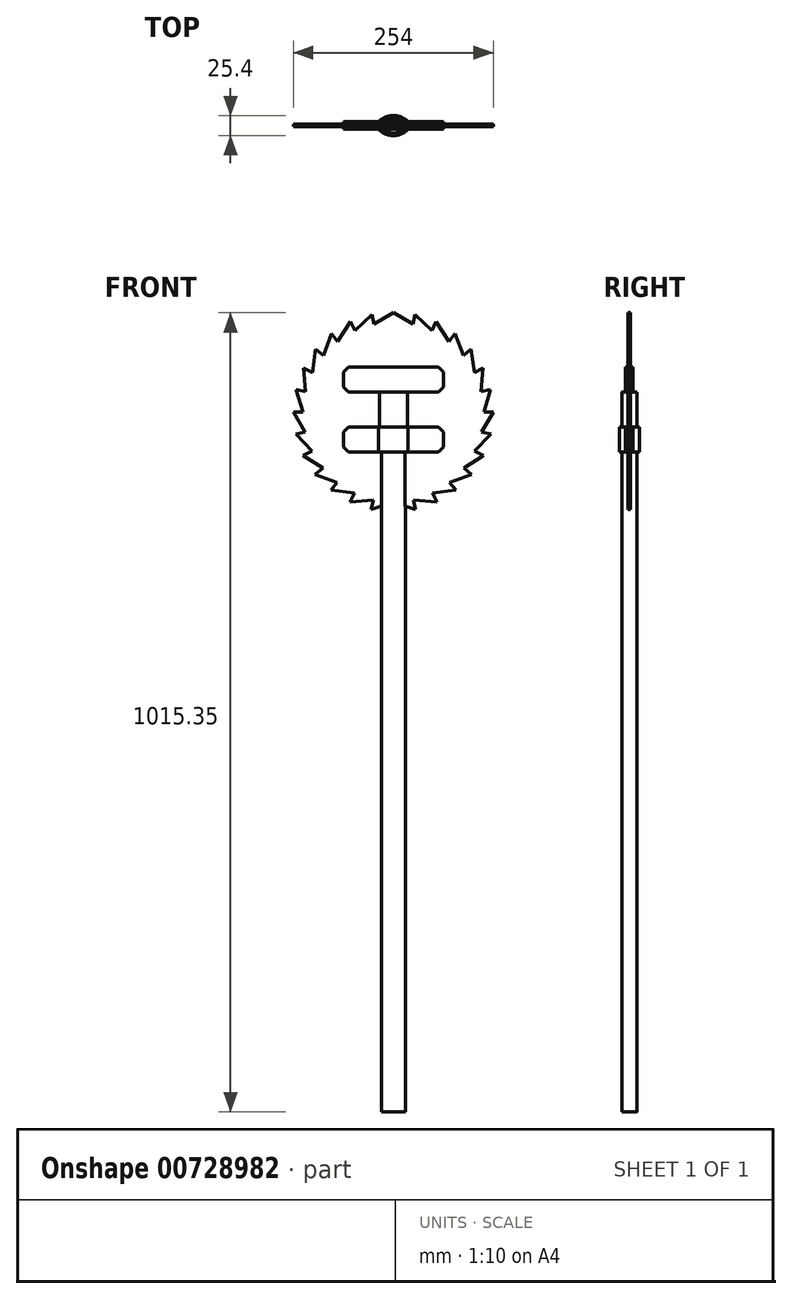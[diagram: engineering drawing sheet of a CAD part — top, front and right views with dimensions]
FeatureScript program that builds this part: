
annotation { "Feature Type Name" : "Feature", "Feature Type Description" : "" }
export const myFeature = defineFeature(function(context is Context, id is Id, definition is map)
    precondition{}
    {
        {
            var Q0;
            Q0=qCreatedBy(makeId("Top.planeOp"),FACE);
            var sketch = newSketch(context, id + "F0", { "sketchPlane" : qUnion([Q0])});
            skArc(sketch, "E0", {"start": v(19.05, 0) * mm, "mid": v(0, 9.53) * mm, "end": v(-19.05, 0) * mm});
            skArc(sketch, "E1", {"start": v(-19.05, 0) * mm, "mid": v(0, -9.53) * mm, "end": v(19.05, 0) * mm});
            skSolve(sketch);
        }
        {
            var Q0;
            Q0 = qSketchRegion(id + "F0", true);
            extrude(context, id + "F1", {"entities" : qUnion([Q0]), "depth" : 914.4 * mm, "offsetDistance" : 25.4 * mm});
        }
        {
            var Q0;
            Q0=qCreatedBy(makeId("Front.planeOp"),FACE);
            var sketch = newSketch(context, id + "F2", { "sketchPlane" : qUnion([Q0])});
            skCircle(sketch, "E2", {"center": v(0, 889) * mm, "radius": 127 * mm});
            skPoint(sketch, "E3", {"position": v(-28.3, 765.2) * mm});
            skPoint(sketch, "E4", {"position": v(0, 762) * mm});
            skPoint(sketch, "E5", {"position": v(-55.17, 774.6) * mm});
            skPoint(sketch, "E6", {"position": v(-79.26, 789.77) * mm});
            skPoint(sketch, "E7", {"position": v(-99.38, 809.93) * mm});
            skPoint(sketch, "E8", {"position": v(-114.5, 834.05) * mm});
            skPoint(sketch, "E9", {"position": v(-123.86, 860.94) * mm});
            skPoint(sketch, "E10", {"position": v(-127, 889.42) * mm});
            skPoint(sketch, "E11", {"position": v(-123.67, 917.89) * mm});
            skPoint(sketch, "E12", {"position": v(-114.13, 944.72) * mm});
            skPoint(sketch, "E13", {"position": v(-98.78, 968.82) * mm});
            skPoint(sketch, "E14", {"position": v(-78.52, 988.82) * mm});
            skPoint(sketch, "E15", {"position": v(-54.3, 1003.8) * mm});
            skPoint(sketch, "E16", {"position": v(-27.36, 1013.02) * mm});
            skPoint(sketch, "E17", {"position": v(1.11, 1016) * mm});
            skLineSegment(sketch, "E18", {"start": v(1.11, 1016) * mm, "end": v(1, 1003.3) * mm});
            skLineSegment(sketch, "E19", {"start": v(-27.36, 1013.02) * mm, "end": v(-24.72, 1001.04) * mm});
            skLineSegment(sketch, "E20", {"start": v(-54.3, 1003.8) * mm, "end": v(-48.87, 992.32) * mm});
            skLineSegment(sketch, "E21", {"start": v(-78.52, 988.82) * mm, "end": v(-70.66, 978.84) * mm});
            skLineSegment(sketch, "E22", {"start": v(-98.78, 968.82) * mm, "end": v(-88.9, 960.84) * mm});
            skLineSegment(sketch, "E23", {"start": v(-114.13, 944.72) * mm, "end": v(-102.96, 939.27) * mm});
            skLineSegment(sketch, "E24", {"start": v(-123.67, 917.89) * mm, "end": v(-111.3, 915) * mm});
            skLineSegment(sketch, "E25", {"start": v(-127, 889.42) * mm, "end": v(-114.84, 889.38) * mm});
            skLineSegment(sketch, "E26", {"start": v(-123.86, 860.94) * mm, "end": v(-111.94, 863.64) * mm});
            skLineSegment(sketch, "E27", {"start": v(-114.5, 834.05) * mm, "end": v(-103.05, 839.55) * mm});
            skLineSegment(sketch, "E28", {"start": v(-99.38, 809.93) * mm, "end": v(-89.44, 817.83) * mm});
            skLineSegment(sketch, "E29", {"start": v(-79.26, 789.77) * mm, "end": v(-71.34, 799.7) * mm});
            skLineSegment(sketch, "E30", {"start": v(-55.17, 774.6) * mm, "end": v(-49.65, 786.05) * mm});
            skLineSegment(sketch, "E31", {"start": v(-28.3, 765.2) * mm, "end": v(-25.46, 777.57) * mm});
            skLineSegment(sketch, "E32", {"start": v(0, 762) * mm, "end": v(0, 774.7) * mm});
            skLineSegment(sketch, "E33", {"start": v(-28.3, 765.2) * mm, "end": v(0, 774.7) * mm});
            skLineSegment(sketch, "E34", {"start": v(-25.46, 777.57) * mm, "end": v(-55.17, 774.6) * mm});
            skLineSegment(sketch, "E35", {"start": v(-49.65, 786.05) * mm, "end": v(-79.26, 789.77) * mm});
            skLineSegment(sketch, "E36", {"start": v(-71.34, 799.7) * mm, "end": v(-99.38, 809.93) * mm});
            skLineSegment(sketch, "E37", {"start": v(-89.44, 817.83) * mm, "end": v(-114.5, 834.05) * mm});
            skLineSegment(sketch, "E38", {"start": v(-103.05, 839.55) * mm, "end": v(-123.86, 860.94) * mm});
            skLineSegment(sketch, "E39", {"start": v(-111.94, 863.64) * mm, "end": v(-127, 889.42) * mm});
            skLineSegment(sketch, "E40", {"start": v(-114.84, 889.38) * mm, "end": v(-123.67, 917.89) * mm});
            skLineSegment(sketch, "E41", {"start": v(-111.3, 915) * mm, "end": v(-114.13, 944.72) * mm});
            skLineSegment(sketch, "E42", {"start": v(-102.96, 939.27) * mm, "end": v(-98.78, 968.82) * mm});
            skLineSegment(sketch, "E43", {"start": v(-88.9, 960.84) * mm, "end": v(-78.52, 988.82) * mm});
            skLineSegment(sketch, "E44", {"start": v(-70.66, 978.84) * mm, "end": v(-54.3, 1003.8) * mm});
            skLineSegment(sketch, "E45", {"start": v(-48.87, 992.32) * mm, "end": v(-27.36, 1013.02) * mm});
            skLineSegment(sketch, "E46", {"start": v(-24.72, 1001.04) * mm, "end": v(1.11, 1016) * mm});
            skPoint(sketch, "E47", {"position": v(1, 1003.3) * mm});
            skLineSegment(sketch, "E48", {"start": v(0, 762) * mm, "end": v(0, 1064.63) * mm, "construction": true});
            skLineSegment(sketch, "E49.MirrorCS", {"start": v(28.3, 765.2) * mm, "end": v(0, 774.7) * mm});
            skLineSegment(sketch, "E50.MirrorCS", {"start": v(25.46, 777.57) * mm, "end": v(55.17, 774.6) * mm});
            skLineSegment(sketch, "E51.MirrorCS", {"start": v(28.3, 765.2) * mm, "end": v(25.46, 777.57) * mm});
            skLineSegment(sketch, "E52.MirrorCS", {"start": v(55.17, 774.6) * mm, "end": v(49.65, 786.05) * mm});
            skLineSegment(sketch, "E53.MirrorCS", {"start": v(49.65, 786.05) * mm, "end": v(79.26, 789.77) * mm});
            skLineSegment(sketch, "E54.MirrorCS", {"start": v(79.26, 789.77) * mm, "end": v(71.34, 799.7) * mm});
            skLineSegment(sketch, "E55.MirrorCS", {"start": v(71.34, 799.7) * mm, "end": v(99.38, 809.93) * mm});
            skLineSegment(sketch, "E56.MirrorCS", {"start": v(99.38, 809.93) * mm, "end": v(89.44, 817.83) * mm});
            skLineSegment(sketch, "E57.MirrorCS", {"start": v(89.44, 817.83) * mm, "end": v(114.5, 834.05) * mm});
            skLineSegment(sketch, "E58.MirrorCS", {"start": v(114.5, 834.05) * mm, "end": v(103.05, 839.55) * mm});
            skLineSegment(sketch, "E59.MirrorCS", {"start": v(103.05, 839.55) * mm, "end": v(123.86, 860.94) * mm});
            skLineSegment(sketch, "E60.MirrorCS", {"start": v(123.86, 860.94) * mm, "end": v(111.94, 863.64) * mm});
            skLineSegment(sketch, "E61.MirrorCS", {"start": v(111.94, 863.64) * mm, "end": v(127, 889.42) * mm});
            skLineSegment(sketch, "E62.MirrorCS", {"start": v(114.84, 889.38) * mm, "end": v(123.67, 917.89) * mm});
            skLineSegment(sketch, "E63.MirrorCS", {"start": v(123.67, 917.89) * mm, "end": v(111.3, 915) * mm});
            skLineSegment(sketch, "E64.MirrorCS", {"start": v(127, 889.42) * mm, "end": v(114.84, 889.38) * mm});
            skLineSegment(sketch, "E65.MirrorCS", {"start": v(111.3, 915) * mm, "end": v(114.13, 944.72) * mm});
            skLineSegment(sketch, "E66.MirrorCS", {"start": v(114.13, 944.72) * mm, "end": v(102.96, 939.27) * mm});
            skLineSegment(sketch, "E67.MirrorCS", {"start": v(102.96, 939.27) * mm, "end": v(98.78, 968.82) * mm});
            skLineSegment(sketch, "E68.MirrorCS", {"start": v(98.78, 968.82) * mm, "end": v(88.9, 960.84) * mm});
            skLineSegment(sketch, "E69.MirrorCS", {"start": v(88.9, 960.84) * mm, "end": v(78.52, 988.82) * mm});
            skLineSegment(sketch, "E70.MirrorCS", {"start": v(78.52, 988.82) * mm, "end": v(70.66, 978.84) * mm});
            skLineSegment(sketch, "E71.MirrorCS", {"start": v(54.3, 1003.8) * mm, "end": v(48.87, 992.32) * mm});
            skLineSegment(sketch, "E72.MirrorCS", {"start": v(70.66, 978.84) * mm, "end": v(54.3, 1003.8) * mm});
            skLineSegment(sketch, "E73.MirrorCS", {"start": v(48.87, 992.32) * mm, "end": v(27.36, 1013.02) * mm});
            skLineSegment(sketch, "E74.MirrorCS", {"start": v(27.36, 1013.02) * mm, "end": v(24.72, 1001.04) * mm});
            skLineSegment(sketch, "E75.MirrorCS", {"start": v(24.72, 1001.04) * mm, "end": v(-1.11, 1016) * mm});
            skLineSegment(sketch, "E76.MirrorCS", {"start": v(-1.11, 1016) * mm, "end": v(-1, 1003.3) * mm});
            skLineSegment(sketch, "E77", {"start": v(-24.72, 1001.04) * mm, "end": v(24.72, 1001.04) * mm, "construction": true});
            skPoint(sketch, "E78.end.orphan", {"position": v(0, 952.5) * mm});
            skSolve(sketch);
        }
        {
            var Q0;
            {var subQ4=sQuery(id+"F2.wireOp",EDGE,"E19");Q0=makeQuery(id+"F2.imprint","IMPRINT",FACE,{"disambiguationData":[TD([[makeQuery(id+"F2.imprint","IMPRINT",EDGE,{"derivedFrom":subQ4}),-1.0]])]});}
            extrude(context, id + "F3", {"entities" : qUnion([Q0]), "depth" : 1.59 * mm, "offsetDistance" : 25.4 * mm, "hasSecondDirection" : true, "secondDirectionOppositeDirection" : true, "secondDirectionDepth" : 1.59 * mm});
        }
        {
            var Q0;
            Q0=qCreatedBy(makeId("Front.planeOp"),FACE);
            var sketch = newSketch(context, id + "F4", { "sketchPlane" : qUnion([Q0])});
            skLineSegment(sketch, "E79.bottom", {"start": v(63.5, 914.4) * mm, "end": v(-63.5, 914.4) * mm});
            skLineSegment(sketch, "E79.top", {"start": v(63.5, 946.15) * mm, "end": v(-63.5, 946.15) * mm});
            skLineSegment(sketch, "E79.left", {"start": v(63.5, 914.4) * mm, "end": v(63.5, 946.15) * mm});
            skLineSegment(sketch, "E79.right", {"start": v(-63.5, 914.4) * mm, "end": v(-63.5, 946.15) * mm});
            skPoint(sketch, "E79.middle", {"position": v(0, 930.28) * mm});
            skLineSegment(sketch, "E80", {"start": v(-57.15, 946.15) * mm, "end": v(-63.5, 939.8) * mm});
            skLineSegment(sketch, "E81", {"start": v(-63.5, 920.75) * mm, "end": v(-57.15, 914.4) * mm});
            skLineSegment(sketch, "E82", {"start": v(57.15, 946.15) * mm, "end": v(63.5, 939.8) * mm});
            skLineSegment(sketch, "E83", {"start": v(63.5, 920.75) * mm, "end": v(57.15, 914.4) * mm});
            skSolve(sketch);
        }
        {
            var Q0;
            {var subQ0=sQuery(id+"F4.wireOp",EDGE,"E80");Q0=makeQuery(id+"F4.imprint","IMPRINT",FACE,{"disambiguationData":[TD([[makeQuery(id+"F4.imprint","IMPRINT",EDGE,{"derivedFrom":subQ0}),1.0]])]});}
            extrude(context, id + "F5", {"entities" : qUnion([Q0]), "depth" : 4.78 * mm, "offsetDistance" : 25.4 * mm, "hasSecondDirection" : true, "secondDirectionOppositeDirection" : true, "secondDirectionDepth" : 4.78 * mm});
        }
        {
            var Q0;
            Q0=qCreatedBy(makeId("Front.planeOp"),FACE);
            var sketch = newSketch(context, id + "F6", { "sketchPlane" : qUnion([Q0])});
            skLineSegment(sketch, "E84.bottom", {"start": v(63.5, 838.2) * mm, "end": v(-63.5, 838.2) * mm});
            skLineSegment(sketch, "E84.top", {"start": v(63.5, 869.95) * mm, "end": v(-63.5, 869.95) * mm});
            skLineSegment(sketch, "E84.left", {"start": v(63.5, 838.2) * mm, "end": v(63.5, 869.95) * mm});
            skLineSegment(sketch, "E84.right", {"start": v(-63.5, 838.2) * mm, "end": v(-63.5, 869.95) * mm});
            skPoint(sketch, "E84.middle", {"position": v(0, 854.08) * mm});
            skLineSegment(sketch, "E85", {"start": v(-57.15, 869.95) * mm, "end": v(-63.5, 863.6) * mm});
            skLineSegment(sketch, "E86", {"start": v(-63.5, 844.55) * mm, "end": v(-57.15, 838.2) * mm});
            skLineSegment(sketch, "E87", {"start": v(57.15, 869.95) * mm, "end": v(63.5, 863.6) * mm});
            skLineSegment(sketch, "E88", {"start": v(57.15, 838.2) * mm, "end": v(63.5, 844.55) * mm});
            skSolve(sketch);
        }
        {
            var Q0;
            {var subQ0=sQuery(id+"F6.wireOp",EDGE,"E85");Q0=makeQuery(id+"F6.imprint","IMPRINT",FACE,{"disambiguationData":[TD([[makeQuery(id+"F6.imprint","IMPRINT",EDGE,{"derivedFrom":subQ0}),1.0]])]});}
            extrude(context, id + "F7", {"entities" : qUnion([Q0]), "operationType" : NewBodyOperationType.ADD, "depth" : 4.78 * mm, "offsetDistance" : 25.4 * mm, "hasSecondDirection" : true, "secondDirectionOppositeDirection" : true, "secondDirectionDepth" : 4.78 * mm});
        }
        {
            var Q0;
            Q0=qCreatedBy(makeId("Top.planeOp"),FACE);
            var sketch = newSketch(context, id + "F8", { "sketchPlane" : qUnion([Q0])});
            skArc(sketch, "E89", {"start": v(22.22, 0) * mm, "mid": v(0, 12.7) * mm, "end": v(-22.22, 0) * mm});
            skArc(sketch, "E90", {"start": v(-22.23, 0) * mm, "mid": v(0, -12.7) * mm, "end": v(22.23, 0) * mm});
            skPoint(sketch, "E90.centerSnap0", {"position": v(0, 12.7) * mm});
            skSolve(sketch);
        }
        {
            var Q0;
            Q0=makeQuery(id+"F8.imprint","IMPRINT",FACE,{"disambiguationData":[TD([[makeQuery(id+"F8.imprint","IMPRINT",EDGE,{"derivedFrom":sQuery(id+"F8.wireOp",EDGE,"E89")}),1.0]])]});
            extrude(context, id + "F9", {"entities" : qUnion([Q0]), "operationType" : NewBodyOperationType.ADD, "depth" : 869.95 * mm, "offsetDistance" : 25.4 * mm, "hasSecondDirection" : true, "secondDirectionOppositeDirection" : false, "secondDirectionDepth" : 838.2 * mm});
        }
        {
            var Q0;
            {var subQ0=sQuery(id+"F0.wireOp",EDGE,"E1");var subQ1=sQuery(id+"F0.wireOp",EDGE,"E0");Q0=makeQuery(id+"F1.opExtrude","SWEPT_EDGE",EDGE,{"disambiguationData":[OSD([subQ1,subQ0]),TDD([makeQuery(id+"F0.imprint","INTERSECT",VERTEX,{"disambiguationData":[OD(1.0)],"derivedFrom":[subQ1,subQ0]})])]});}
            var Q1;
            {var subQ0=sQuery(id+"F0.wireOp",EDGE,"E1");var subQ1=sQuery(id+"F0.wireOp",EDGE,"E0");Q1=makeQuery(id+"F1.opExtrude","SWEPT_EDGE",EDGE,{"disambiguationData":[OSD([subQ1,subQ0]),TDD([makeQuery(id+"F0.imprint","INTERSECT",VERTEX,{"disambiguationData":[OD(0.0)],"derivedFrom":[subQ1,subQ0]})])]});}
            fillet(context, id + "F10", {"entities" : qUnion([Q0, Q1]), "radius" : 7.62 * mm, "tangentPropagation" : true, "allowEdgeOverflow" : false});
        }
    });
